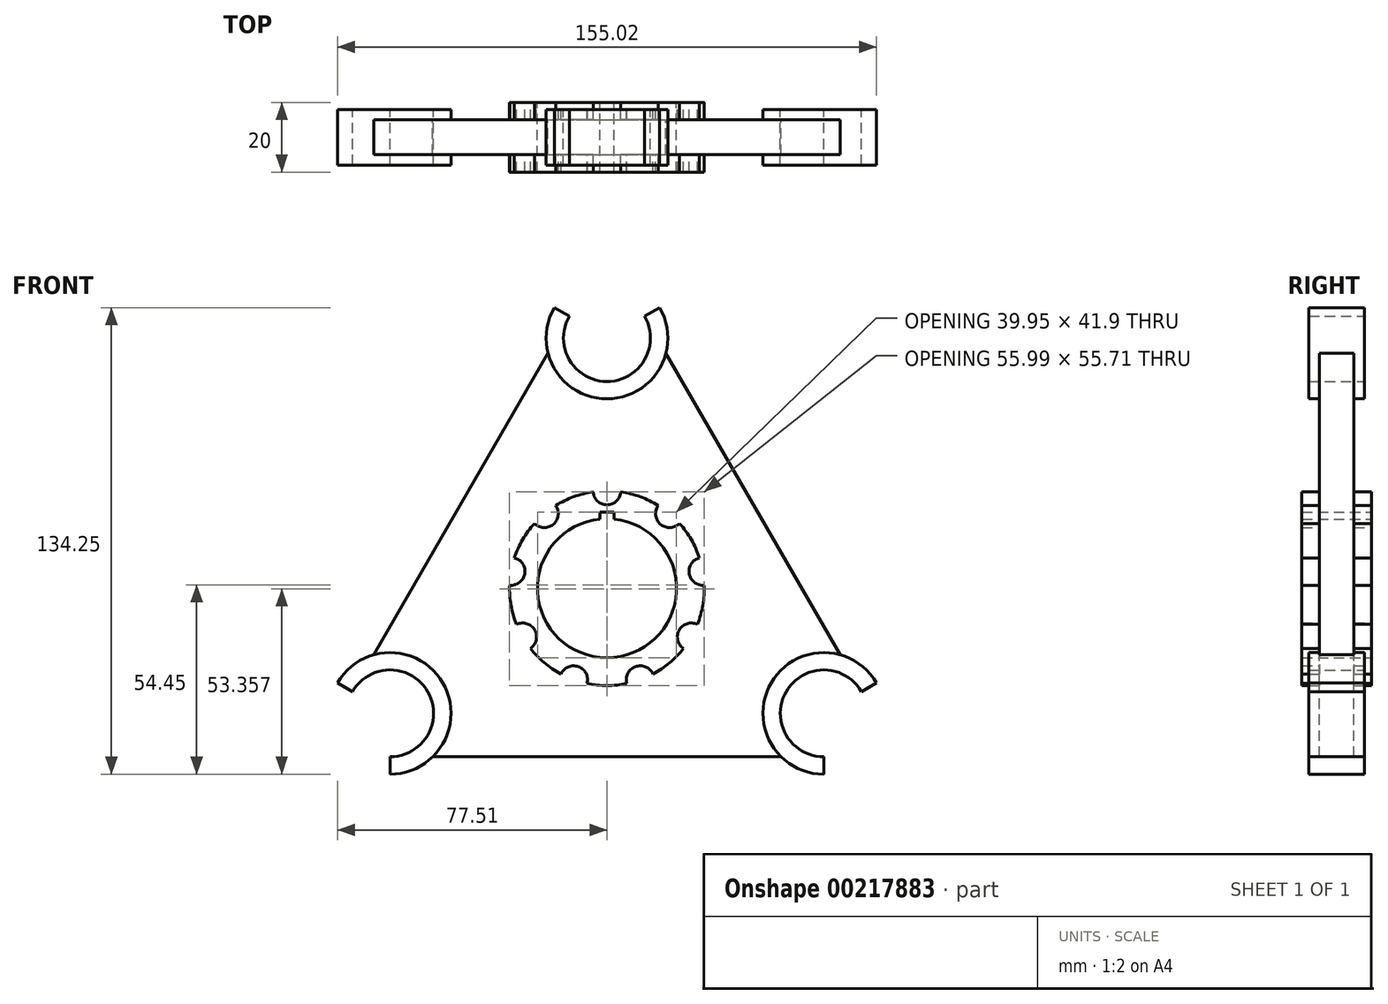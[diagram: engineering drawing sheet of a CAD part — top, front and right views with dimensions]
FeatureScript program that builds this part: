
annotation { "Feature Type Name" : "Feature", "Feature Type Description" : "" }
export const myFeature = defineFeature(function(context is Context, id is Id, definition is map)
    precondition{}
    {
        {
            var Q0;
            Q0=qCreatedBy(makeId("Front.planeOp"),FACE);
            var sketch = newSketch(context, id + "F0", { "sketchPlane" : qUnion([Q0])});
            skArc(sketch, "E0", {"start": v(-15.16, 80.75) * mm, "mid": v(0, 54.5) * mm, "end": v(15.16, 80.75) * mm});
            skCircle(sketch, "E1", {"center": v(0, 0) * mm, "radius": 72 * mm, "construction": true});
            skArc(sketch, "E2", {"start": v(-2, 19.9) * mm, "mid": v(0, -20) * mm, "end": v(2, 19.9) * mm});
            skLineSegment(sketch, "E3", {"start": v(-93.67, 0) * mm, "end": v(88.37, 0) * mm, "construction": true});
            skArc(sketch, "E4", {"start": v(-10.83, 78.25) * mm, "mid": v(0, 59.5) * mm, "end": v(10.83, 78.25) * mm});
            skLineSegment(sketch, "E5", {"start": v(10.83, 78.25) * mm, "end": v(15.16, 80.75) * mm});
            skLineSegment(sketch, "E6", {"start": v(-10.83, 78.25) * mm, "end": v(-15.16, 80.75) * mm});
            skArc(sketch, "E7.1.0", {"start": v(-62.35, -48.5) * mm, "mid": v(-51.53, -29.75) * mm, "end": v(-73.18, -29.75) * mm});
            skArc(sketch, "E7.1.1", {"start": v(-62.35, -53.5) * mm, "mid": v(-47.2, -27.25) * mm, "end": v(-77.5, -27.25) * mm});
            skLineSegment(sketch, "E7.1.2", {"start": v(-62.35, -48.5) * mm, "end": v(-62.35, -53.5) * mm});
            skLineSegment(sketch, "E7.1.3", {"start": v(-73.18, -29.75) * mm, "end": v(-77.5, -27.25) * mm});
            skArc(sketch, "E7.2.0", {"start": v(73.18, -29.75) * mm, "mid": v(51.53, -29.75) * mm, "end": v(62.35, -48.5) * mm});
            skArc(sketch, "E7.2.1", {"start": v(77.5, -27.25) * mm, "mid": v(47.2, -27.25) * mm, "end": v(62.35, -53.5) * mm});
            skLineSegment(sketch, "E7.2.2", {"start": v(73.18, -29.75) * mm, "end": v(77.5, -27.25) * mm});
            skLineSegment(sketch, "E7.2.3", {"start": v(62.35, -48.5) * mm, "end": v(62.35, -53.5) * mm});
            skLineSegment(sketch, "E8", {"start": v(-16.95, 67.64) * mm, "end": v(-67.06, -19.14) * mm});
            skLineSegment(sketch, "E9", {"start": v(16.95, 67.64) * mm, "end": v(67.06, -19.14) * mm});
            skLineSegment(sketch, "E10", {"start": v(-50.1, -48.5) * mm, "end": v(50.1, -48.5) * mm});
            skArc(sketch, "E11", {"start": v(-3.99, 27.71) * mm, "mid": v(-9.58, 26.31) * mm, "end": v(-14.76, 23.8) * mm});
            skArc(sketch, "E12", {"start": v(-3.99, 27.71) * mm, "mid": v(0, 24) * mm, "end": v(3.99, 27.71) * mm});
            skLineSegment(sketch, "E13", {"start": v(0, 72) * mm, "end": v(0, -63.22) * mm, "construction": true});
            skArc(sketch, "E14.1.0", {"start": v(-20.87, 18.67) * mm, "mid": v(-15.43, 18.39) * mm, "end": v(-14.76, 23.8) * mm});
            skArc(sketch, "E14.2.0", {"start": v(-27.99, 0.88) * mm, "mid": v(-23.64, 4.17) * mm, "end": v(-26.6, 8.74) * mm});
            skArc(sketch, "E15.2.3.0", {"start": v(-22, -17.31) * mm, "mid": v(-20.78, -12) * mm, "end": v(-26, -10.4) * mm});
            skArc(sketch, "E15.2.4.0", {"start": v(-5.73, -27.4) * mm, "mid": v(-8.2, -22.55) * mm, "end": v(-13.23, -24.68) * mm});
            skArc(sketch, "E15.2.5.0", {"start": v(13.23, -24.68) * mm, "mid": v(8.2, -22.55) * mm, "end": v(5.73, -27.4) * mm});
            skArc(sketch, "E15.2.6.0", {"start": v(26, -10.4) * mm, "mid": v(20.78, -12) * mm, "end": v(22, -17.31) * mm});
            skArc(sketch, "E15.2.7.0", {"start": v(26.6, 8.74) * mm, "mid": v(23.64, 4.17) * mm, "end": v(27.99, 0.88) * mm});
            skArc(sketch, "E15.2.8.0", {"start": v(14.76, 23.8) * mm, "mid": v(15.43, 18.39) * mm, "end": v(20.87, 18.67) * mm});
            skArc(sketch, "E16.trimOffspring", {"start": v(14.76, 23.8) * mm, "mid": v(9.58, 26.31) * mm, "end": v(3.99, 27.71) * mm});
            skArc(sketch, "E17.trimOffspring", {"start": v(26.6, 8.74) * mm, "mid": v(24.25, 14) * mm, "end": v(20.87, 18.67) * mm});
            skArc(sketch, "E18.trimOffspring", {"start": v(26, -10.4) * mm, "mid": v(27.57, -4.86) * mm, "end": v(27.99, 0.88) * mm});
            skArc(sketch, "E19.trimOffspring", {"start": v(13.23, -24.68) * mm, "mid": v(18, -21.45) * mm, "end": v(22, -17.31) * mm});
            skArc(sketch, "E20.trimOffspring", {"start": v(-5.73, -27.4) * mm, "mid": v(0, -28) * mm, "end": v(5.73, -27.4) * mm});
            skArc(sketch, "E21.trimOffspring", {"start": v(-22, -17.31) * mm, "mid": v(-18, -21.45) * mm, "end": v(-13.23, -24.68) * mm});
            skArc(sketch, "E22.trimOffspring", {"start": v(-27.99, 0.88) * mm, "mid": v(-27.57, -4.86) * mm, "end": v(-26, -10.4) * mm});
            skArc(sketch, "E23.trimOffspring", {"start": v(-20.87, 18.67) * mm, "mid": v(-24.25, 14) * mm, "end": v(-26.6, 8.74) * mm});
            skLineSegment(sketch, "E24", {"start": v(-2, 19.9) * mm, "end": v(-2, 21.9) * mm});
            skLineSegment(sketch, "E25", {"start": v(-2, 21.9) * mm, "end": v(2, 21.9) * mm});
            skLineSegment(sketch, "E26", {"start": v(2, 21.9) * mm, "end": v(2, 19.9) * mm});
            skSolve(sketch);
        }
        {
            var Q0;
            Q0=makeQuery(id+"F0.imprint","IMPRINT",FACE,{"disambiguationData":[TD([[makeQuery(id+"F0.imprint","IMPRINT",EDGE,{"derivedFrom":sQuery(id+"F0.wireOp",EDGE,"E2")}),-1.0]])]});
            extrude(context, id + "F1", {"entities" : qUnion([Q0]), "endBound" : BoundingType.SYMMETRIC, "depth" : 20 * mm});
        }
        {
            var Q0;
            Q0=makeQuery(id+"F0.imprint","IMPRINT",FACE,{"disambiguationData":[TD([[makeQuery(id+"F0.imprint","IMPRINT",EDGE,{"derivedFrom":sQuery(id+"F0.wireOp",EDGE,"E4")}),-1.0]])]});
            var Q1;
            Q1=makeQuery(id+"F0.imprint","IMPRINT",FACE,{"disambiguationData":[TD([[makeQuery(id+"F0.imprint","IMPRINT",EDGE,{"derivedFrom":sQuery(id+"F0.wireOp",EDGE,"E7.1.0")}),-1.0]])]});
            var Q2;
            Q2=makeQuery(id+"F0.imprint","IMPRINT",FACE,{"disambiguationData":[TD([[makeQuery(id+"F0.imprint","IMPRINT",EDGE,{"derivedFrom":sQuery(id+"F0.wireOp",EDGE,"E7.2.0")}),-1.0]])]});
            extrude(context, id + "F2", {"entities" : qUnion([Q0, Q1, Q2]), "endBound" : BoundingType.SYMMETRIC, "depth" : 16 * mm});
        }
        {
            var Q0;
            {var subQ0=sQuery(id+"F0.wireOp",EDGE,"E8");Q0=makeQuery(id+"F0.imprint","IMPRINT",FACE,{"disambiguationData":[TD([[makeQuery(id+"F0.imprint","IMPRINT",EDGE,{"derivedFrom":subQ0}),1.0]])]});}
            extrude(context, id + "F3", {"entities" : qUnion([Q0]), "operationType" : NewBodyOperationType.ADD, "endBound" : BoundingType.SYMMETRIC, "depth" : 10 * mm});
        }
    });
